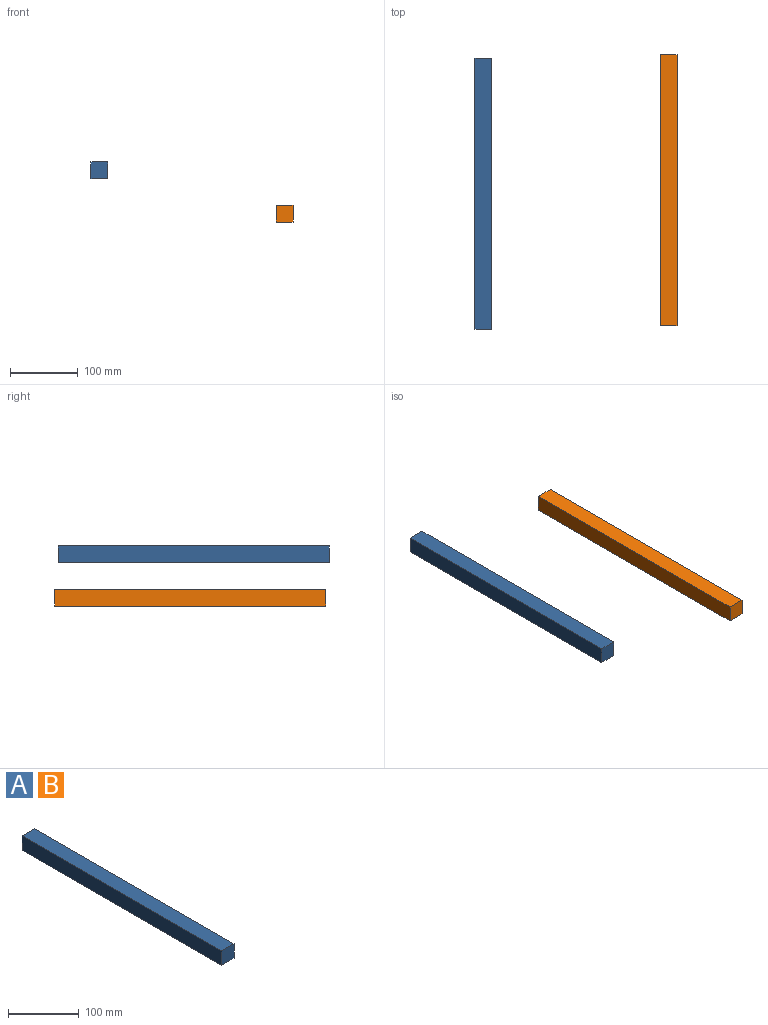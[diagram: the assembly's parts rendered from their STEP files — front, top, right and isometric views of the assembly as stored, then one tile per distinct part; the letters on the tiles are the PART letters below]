
ASSEMBLY  parts=2 mates=2
PART A: 6 faces, bbox 25x400x25 mm
  f0: plane 400x25mm, normal (-1,0,0), area 10000mm2, adj f1,f3,f4,f5
  f1: plane 400x25mm, normal (0,0,-1), area 10000mm2, adj f0,f2,f4,f5
  f2: plane 400x25mm, normal (1,0,0), area 10000mm2, adj f1,f3,f4,f5
  f3: plane 400x25mm, normal (0,0,1), area 10000mm2, adj f0,f2,f4,f5
  f4: plane 25x25mm, normal (0,1,0), area 625mm2, adj f0,f1,f2,f3
  f5: plane 25x25mm, normal (0,-1,0), area 625mm2, adj f0,f1,f2,f3
PART B: same geometry as A
PLACE A t=(-273.13,-5.4,63.76)mm
PLACE B at identity
MATE parallel B.f0 <-> A.f2  axis (-1,0,0) through (0,200,12.5)mm
MATE parallel B.f4 <-> A.f4  axis (0,1,0) through (12.5,400,12.5)mm
